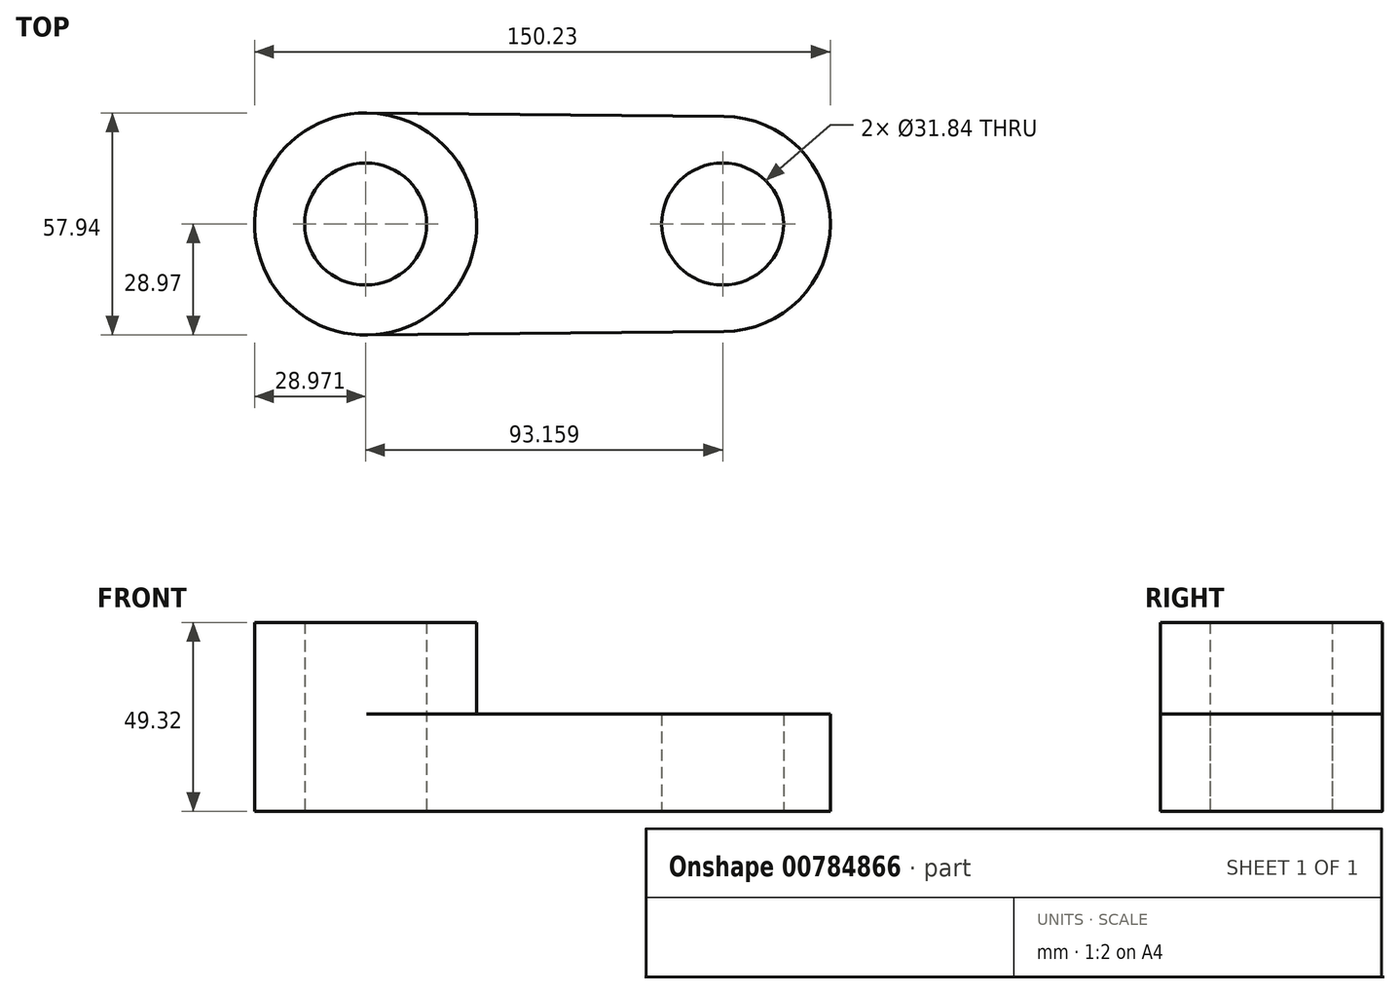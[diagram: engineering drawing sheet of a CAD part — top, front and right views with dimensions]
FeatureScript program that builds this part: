
annotation { "Feature Type Name" : "Feature", "Feature Type Description" : "" }
export const myFeature = defineFeature(function(context is Context, id is Id, definition is map)
    precondition{}
    {
        {
            var Q0;
            Q0=qCreatedBy(makeId("Top.planeOp"),FACE);
            var sketch = newSketch(context, id + "F0", { "sketchPlane" : qUnion([Q0])});
            skCircle(sketch, "E0", {"center": v(-46.58, 0) * mm, "radius": 15.92 * mm});
            skCircle(sketch, "E1", {"center": v(46.58, 0) * mm, "radius": 15.92 * mm});
            skArc(sketch, "E2", {"start": v(-46.3, 28.97) * mm, "mid": v(-75.55, 0) * mm, "end": v(-46.3, -28.97) * mm});
            skArc(sketch, "E3", {"start": v(46.84, -28.1) * mm, "mid": v(74.68, 0) * mm, "end": v(46.84, 28.1) * mm});
            skLineSegment(sketch, "E4", {"start": v(-46.3, 28.97) * mm, "end": v(46.84, 28.1) * mm});
            skLineSegment(sketch, "E5", {"start": v(46.84, -28.1) * mm, "end": v(-46.3, -28.97) * mm});
            skArc(sketch, "E6", {"start": v(-46.3, -28.97) * mm, "mid": v(-17.6, 0) * mm, "end": v(-46.3, 28.97) * mm});
            skSolve(sketch);
        }
        {
            var Q0;
            Q0=makeQuery(id+"F0.imprint","IMPRINT",FACE,{"disambiguationData":[TD([[makeQuery(id+"F0.imprint","IMPRINT",EDGE,{"derivedFrom":sQuery(id+"F0.wireOp",EDGE,"E0")}),-1.0]])]});
            var Q1;
            Q1=makeQuery(id+"F0.imprint","IMPRINT",FACE,{"disambiguationData":[TD([[makeQuery(id+"F0.imprint","IMPRINT",EDGE,{"derivedFrom":sQuery(id+"F0.wireOp",EDGE,"E1")}),-1.0]])]});
            extrude(context, id + "F1", {"entities" : qUnion([Q0, Q1]), "depth" : 25.4 * mm, "offsetDistance" : 25.4 * mm});
        }
        {
            var Q0;
            Q0=makeQuery(id+"F0.imprint","IMPRINT",FACE,{"disambiguationData":[TD([[makeQuery(id+"F0.imprint","IMPRINT",EDGE,{"derivedFrom":sQuery(id+"F0.wireOp",EDGE,"E0")}),-1.0]])]});
            extrude(context, id + "F2", {"entities" : qUnion([Q0]), "operationType" : NewBodyOperationType.ADD, "depth" : 49.32 * mm});
        }
    });
